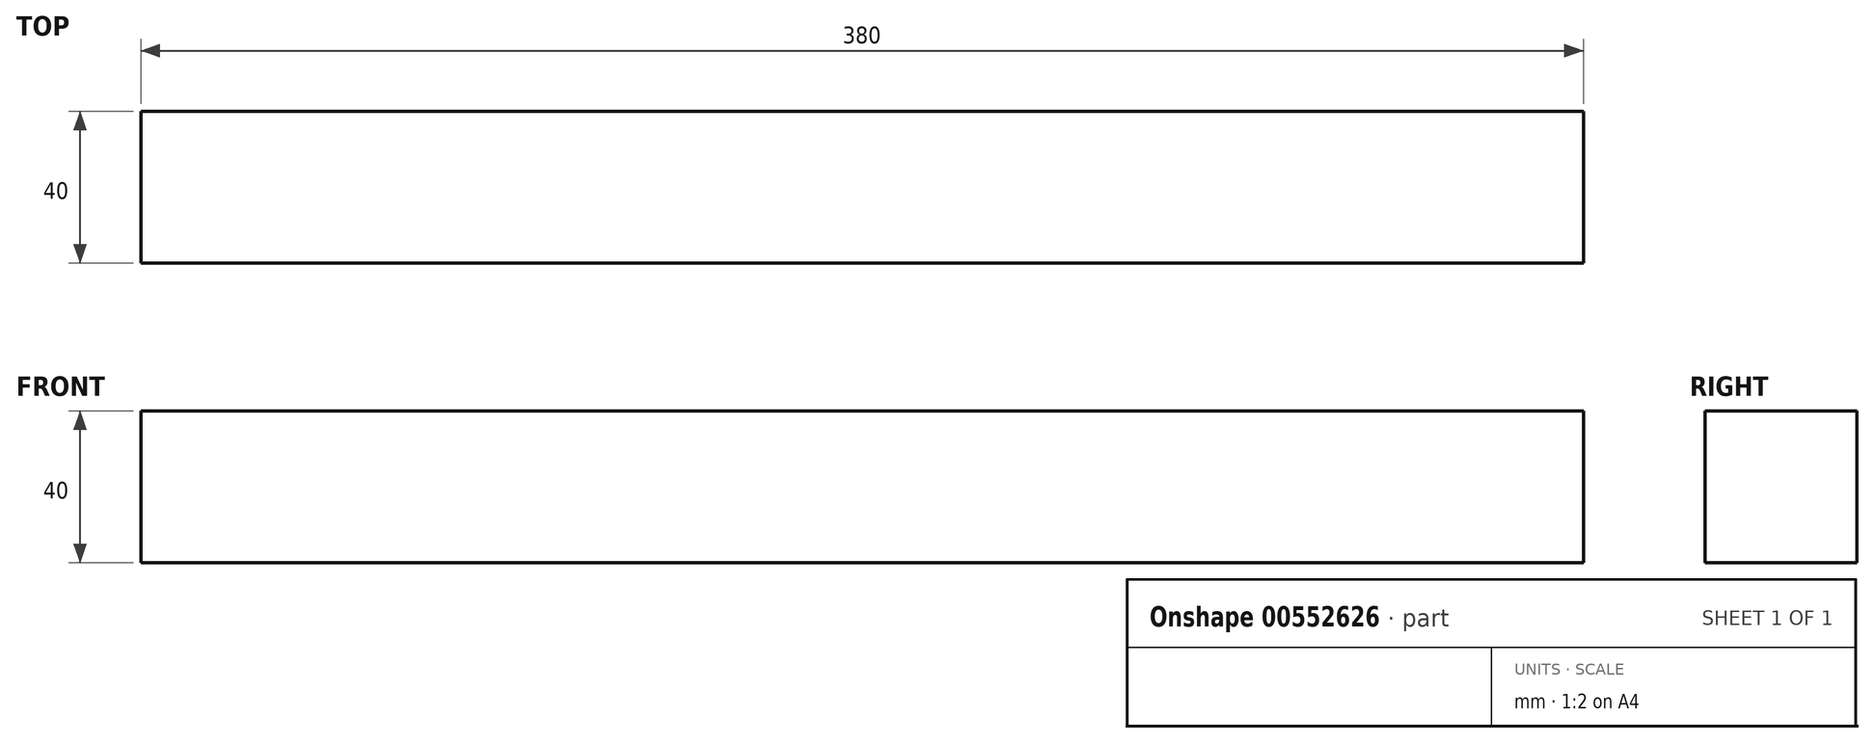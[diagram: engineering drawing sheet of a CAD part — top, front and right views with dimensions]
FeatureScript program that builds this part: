
annotation { "Feature Type Name" : "Feature", "Feature Type Description" : "" }
export const myFeature = defineFeature(function(context is Context, id is Id, definition is map)
    precondition{}
    {
        {
            var Q0;
            Q0=qCreatedBy(makeId("Front.planeOp"),FACE);
            var sketch = newSketch(context, id + "F0", { "sketchPlane" : qUnion([Q0])});
            skLineSegment(sketch, "E0.bottom", {"start": v(-190, 20) * mm, "end": v(190, 20) * mm});
            skLineSegment(sketch, "E0.top", {"start": v(-190, -20) * mm, "end": v(190, -20) * mm});
            skLineSegment(sketch, "E0.left", {"start": v(-190, 20) * mm, "end": v(-190, -20) * mm});
            skLineSegment(sketch, "E0.right", {"start": v(190, 20) * mm, "end": v(190, -20) * mm});
            skPoint(sketch, "E0.middle", {"position": v(0, 0) * mm});
            skSolve(sketch);
        }
        {
            var Q0;
            Q0 = qSketchRegion(id + "F0", true);
            extrude(context, id + "F1", {"entities" : qUnion([Q0]), "depth" : 40 * mm, "offsetDistance" : 25 * mm});
        }
    });
